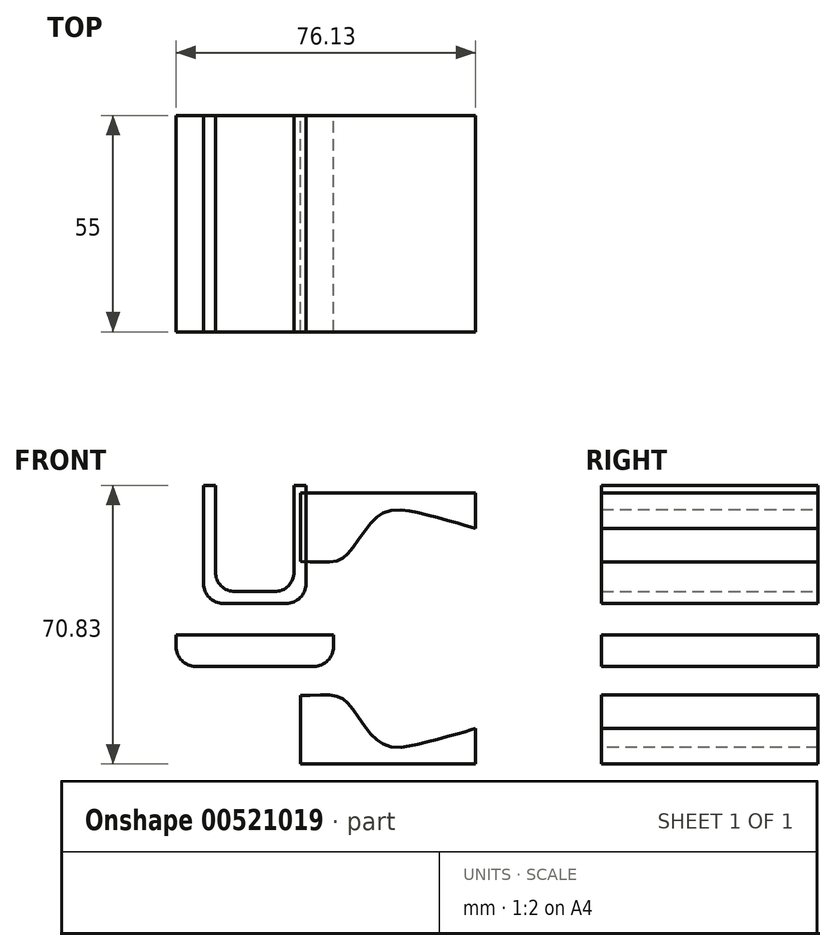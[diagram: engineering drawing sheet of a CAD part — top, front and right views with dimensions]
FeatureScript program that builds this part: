
annotation { "Feature Type Name" : "Feature", "Feature Type Description" : "" }
export const myFeature = defineFeature(function(context is Context, id is Id, definition is map)
    precondition{}
    {
        {
            var Q0;
            Q0=qCreatedBy(makeId("Front.planeOp"),FACE);
            var sketch = newSketch(context, id + "F0", { "sketchPlane" : qUnion([Q0])});
            skLineSegment(sketch, "E0.bottom", {"start": v(-10, 9.37) * mm, "end": v(10, 9.37) * mm});
            skLineSegment(sketch, "E0.top", {"start": v(-10, 6.37) * mm, "end": v(10, 6.37) * mm});
            skLineSegment(sketch, "E0.left", {"start": v(-10, 9.37) * mm, "end": v(-10, 6.37) * mm});
            skLineSegment(sketch, "E0.right", {"start": v(10, 9.37) * mm, "end": v(10, 6.37) * mm});
            skLineSegment(sketch, "E1.bottom", {"start": v(-4, 6.37) * mm, "end": v(4, 6.37) * mm});
            skLineSegment(sketch, "E1.top", {"start": v(-4, -1.63) * mm, "end": v(4, -1.63) * mm});
            skLineSegment(sketch, "E1.left", {"start": v(-4, 6.37) * mm, "end": v(-4, -1.63) * mm});
            skLineSegment(sketch, "E1.right", {"start": v(4, 6.37) * mm, "end": v(4, -1.63) * mm});
            skLineSegment(sketch, "E2.bottom", {"start": v(-20, -9.63) * mm, "end": v(20, -9.63) * mm});
            skLineSegment(sketch, "E2.top", {"start": v(-20, -1.63) * mm, "end": v(20, -1.63) * mm});
            skLineSegment(sketch, "E2.left", {"start": v(-20, -9.63) * mm, "end": v(-20, -1.63) * mm});
            skLineSegment(sketch, "E2.right", {"start": v(20, -9.63) * mm, "end": v(20, -1.63) * mm});
            skLineSegment(sketch, "E3.bottom", {"start": v(10, 6.37) * mm, "end": v(13, 6.37) * mm});
            skLineSegment(sketch, "E3.top", {"start": v(10, 36.37) * mm, "end": v(13, 36.37) * mm});
            skLineSegment(sketch, "E3.left", {"start": v(10, 6.37) * mm, "end": v(10, 36.37) * mm});
            skLineSegment(sketch, "E3.right", {"start": v(13, 6.37) * mm, "end": v(13, 36.37) * mm});
            skLineSegment(sketch, "E4.bottom", {"start": v(-10, 6.37) * mm, "end": v(-13, 6.37) * mm});
            skLineSegment(sketch, "E4.top", {"start": v(-10, 36.37) * mm, "end": v(-13, 36.37) * mm});
            skLineSegment(sketch, "E4.left", {"start": v(-10, 6.37) * mm, "end": v(-10, 36.37) * mm});
            skLineSegment(sketch, "E4.right", {"start": v(-13, 6.37) * mm, "end": v(-13, 36.37) * mm});
            skSolve(sketch);
        }
        {
            var Q0;
            Q0=makeQuery(id+"F0.imprint","IMPRINT",FACE,{"disambiguationData":[TD([[makeQuery(id+"F0.imprint","IMPRINT",EDGE,{"derivedFrom":sQuery(id+"F0.wireOp",EDGE,"E2.bottom")}),1.0]])]});
            var Q1;
            Q1=makeQuery(id+"F0.imprint","IMPRINT",FACE,{"disambiguationData":[TD([[makeQuery(id+"F0.imprint","IMPRINT",EDGE,{"derivedFrom":sQuery(id+"F0.wireOp",EDGE,"E1.bottom")}),-1.0]])]});
            var Q2;
            {var subQ2=sQuery(id+"F0.wireOp",EDGE,"E0.bottom");Q2=makeQuery(id+"F0.imprint","IMPRINT",FACE,{"disambiguationData":[TD([[makeQuery(id+"F0.imprint","IMPRINT",EDGE,{"derivedFrom":subQ2}),-1.0]])]});}
            var Q3;
            {var subQ3=sQuery(id+"F0.wireOp",EDGE,"E3.bottom");Q3=makeQuery(id+"F0.imprint","IMPRINT",FACE,{"disambiguationData":[TD([[makeQuery(id+"F0.imprint","IMPRINT",EDGE,{"derivedFrom":subQ3}),1.0]])]});}
            var Q4;
            {var subQ3=sQuery(id+"F0.wireOp",EDGE,"E4.bottom");Q4=makeQuery(id+"F0.imprint","IMPRINT",FACE,{"disambiguationData":[TD([[makeQuery(id+"F0.imprint","IMPRINT",EDGE,{"derivedFrom":subQ3}),-1.0]])]});}
            extrude(context, id + "F1", {"entities" : qUnion([Q0, Q1, Q2, Q3, Q4]), "endBound" : BoundingType.SYMMETRIC, "depth" : 55 * mm, "offsetDistance" : 25 * mm});
        }
        {
            var Q0;
            Q0=makeQuery(id+"F1.opExtrude","SWEPT_EDGE",EDGE,{"disambiguationData":[OSD([sQuery(id+"F0.wireOp",EDGE,"E0.bottom"),sQuery(id+"F0.wireOp",EDGE,"E4.left")])]});
            var Q1;
            Q1=makeQuery(id+"F1.opExtrude","SWEPT_EDGE",EDGE,{"disambiguationData":[OSD([sQuery(id+"F0.wireOp",EDGE,"E0.bottom"),sQuery(id+"F0.wireOp",EDGE,"E3.left")])]});
            var Q2;
            Q2=makeQuery(id+"F1.opExtrude","SWEPT_EDGE",EDGE,{"disambiguationData":[OSD([sQuery(id+"F0.wireOp",EDGE,"E4.bottom"),sQuery(id+"F0.wireOp",EDGE,"E4.right")])]});
            var Q3;
            Q3=makeQuery(id+"F1.opExtrude","SWEPT_EDGE",EDGE,{"disambiguationData":[OSD([sQuery(id+"F0.wireOp",EDGE,"E3.bottom"),sQuery(id+"F0.wireOp",EDGE,"E3.right")])]});
            var Q4;
            Q4=makeQuery(id+"F1.opExtrude","SWEPT_EDGE",EDGE,{"disambiguationData":[OSD([sQuery(id+"F0.wireOp",EDGE,"E2.bottom"),sQuery(id+"F0.wireOp",EDGE,"E2.left")])]});
            var Q5;
            Q5=makeQuery(id+"F1.opExtrude","SWEPT_EDGE",EDGE,{"disambiguationData":[OSD([sQuery(id+"F0.wireOp",EDGE,"E2.bottom"),sQuery(id+"F0.wireOp",EDGE,"E2.right")])]});
            fillet(context, id + "F2", {"entities" : qUnion([Q0, Q1, Q2, Q3, Q4, Q5]), "radius" : 5 * mm, "tangentPropagation" : true, "allowEdgeOverflow" : false});
        }
        {
            var Q0;
            Q0 = qSketchRegion(id + "F0", true);
            var sketch = newSketch(context, id + "F3", { "sketchPlane" : qUnion([Q0])});
            skFitSpline(sketch, "E5", {"points": [v(-30.87, 10.53) * mm, v(11.63, 14) * mm, v(24.13, 15.5) * mm, v(32.8, 25.83) * mm, v(39.46, 26.75) * mm, v(53.8, 23) * mm, v(56.13, 22) * mm, v(57.13, 0) * mm], "startDerivative": vector(208.32, 11.15) * mm, "endDerivative": vector(-6.45, -276.73) * mm});
            skLineSegment(sketch, "E6", {"start": v(-30.87, 10.53) * mm, "end": v(-30.87, 0) * mm});
            skLineSegment(sketch, "E7", {"start": v(-30.87, 0) * mm, "end": v(57.13, 0) * mm});
            skFitSpline(sketch, "E8.MirrorCS", {"points": [v(-30.87, -10.53) * mm, v(11.63, -14) * mm, v(24.13, -15.5) * mm, v(32.8, -25.83) * mm, v(39.46, -26.75) * mm, v(53.8, -23) * mm, v(56.13, -22) * mm, v(57.13, 0) * mm], "startDerivative": vector(208.32, -11.15) * mm, "endDerivative": vector(-6.45, 276.73) * mm});
            skLineSegment(sketch, "E9.MirrorCS", {"start": v(-30.87, -10.53) * mm, "end": v(-30.87, 0) * mm});
            skLineSegment(sketch, "E10", {"start": v(-41.52, 0) * mm, "end": v(90.5, 0) * mm, "construction": true});
            skPoint(sketch, "E11.end.orphan", {"position": v(-30.87, 22.53) * mm});
            skLineSegment(sketch, "E12.bottom", {"start": v(11.63, 14) * mm, "end": v(20.1, 14) * mm});
            skLineSegment(sketch, "E12.top", {"start": v(11.63, 34.46) * mm, "end": v(56.13, 34.46) * mm});
            skLineSegment(sketch, "E12.left", {"start": v(11.63, 14) * mm, "end": v(11.63, 34.46) * mm});
            skLineSegment(sketch, "E12.right", {"start": v(56.13, 22) * mm, "end": v(56.13, 34.46) * mm});
            skLineSegment(sketch, "E13.MirrorCS", {"start": v(11.63, -34.46) * mm, "end": v(56.13, -34.46) * mm});
            skLineSegment(sketch, "E14.MirrorCS", {"start": v(56.13, -22) * mm, "end": v(56.13, -34.46) * mm});
            skLineSegment(sketch, "E15.MirrorCS", {"start": v(11.63, -14) * mm, "end": v(11.63, -34.46) * mm});
            skFitSpline(sketch, "E16.0", {"points": [v(-31.03, 13.53) * mm, v(-26.74, 13.76) * mm, v(-20.46, 14.26) * mm, v(-12.55, 15.05) * mm, v(-6.9, 15.64) * mm, v(-1.58, 16.2) * mm, v(2.57, 16.57) * mm, v(5.69, 16.8) * mm, v(7.92, 16.92) * mm, v(9.7, 16.98) * mm, v(11.07, 17) * mm, v(12.41, 17) * mm, v(13.97, 16.96) * mm, v(15.67, 16.9) * mm, v(17.19, 16.85) * mm, v(18.52, 16.86) * mm, v(19.66, 16.95) * mm, v(20.62, 17.12) * mm, v(21.42, 17.38) * mm, v(22.02, 17.69) * mm, v(22.49, 18) * mm, v(22.87, 18.32) * mm, v(23.29, 18.7) * mm, v(23.86, 19.3) * mm, v(24.61, 20.17) * mm, v(25.53, 21.4) * mm, v(26.47, 22.7) * mm, v(27.42, 24.06) * mm, v(28.39, 25.4) * mm, v(29.4, 26.68) * mm, v(30.33, 27.67) * mm, v(31.17, 28.4) * mm, v(31.85, 28.88) * mm, v(32.56, 29.3) * mm, v(33.56, 29.74) * mm, v(34.87, 30.08) * mm, v(36.4, 30.18) * mm, v(37.85, 30.08) * mm, v(39.06, 29.89) * mm, v(40.05, 29.7) * mm, v(41.07, 29.48) * mm, v(42.43, 29.17) * mm, v(44.14, 28.75) * mm, v(45.9, 28.3) * mm, v(47.66, 27.83) * mm, v(49.37, 27.36) * mm, v(51, 26.91) * mm, v(52.23, 26.56) * mm, v(53.13, 26.3) * mm, v(53.75, 26.13) * mm, v(54.31, 25.97) * mm, v(54.8, 25.83) * mm, v(55.26, 25.7) * mm, v(55.7, 25.58) * mm, v(56.14, 25.43) * mm, v(56.62, 25.24) * mm, v(57.13, 24.99) * mm, v(57.67, 24.65) * mm, v(58.18, 24.22) * mm, v(58.6, 23.74) * mm, v(58.98, 23.2) * mm, v(59.38, 22.46) * mm, v(59.72, 21.5) * mm, v(59.98, 20.3) * mm, v(60.15, 18.93) * mm, v(60.3, 16.82) * mm, v(60.36, 13.45) * mm, v(60.3, 7.84) * mm, v(60.2, 2.82) * mm, v(60.13, -0.07) * mm]});
            skPoint(sketch, "E17", {"position": v(56.13, 25.43) * mm});
            skFitSpline(sketch, "E18.trimOffspring", {"points": [v(-31.03, 13.53) * mm, v(-26.74, 13.76) * mm, v(-20.46, 14.26) * mm, v(-12.55, 15.05) * mm, v(-6.9, 15.64) * mm, v(-1.58, 16.2) * mm, v(2.57, 16.57) * mm, v(5.69, 16.8) * mm, v(7.92, 16.92) * mm, v(9.7, 16.98) * mm, v(11.07, 17) * mm, v(12.41, 17) * mm, v(13.97, 16.96) * mm, v(15.67, 16.9) * mm, v(17.19, 16.85) * mm, v(18.52, 16.86) * mm, v(19.66, 16.95) * mm, v(20.62, 17.12) * mm, v(21.42, 17.38) * mm, v(22.02, 17.69) * mm, v(22.49, 18) * mm, v(22.87, 18.32) * mm, v(23.29, 18.7) * mm, v(23.86, 19.3) * mm, v(24.61, 20.17) * mm, v(25.53, 21.4) * mm, v(26.47, 22.7) * mm, v(27.42, 24.06) * mm, v(28.39, 25.4) * mm, v(29.4, 26.68) * mm, v(30.33, 27.67) * mm, v(31.17, 28.4) * mm, v(31.85, 28.88) * mm, v(32.56, 29.3) * mm, v(33.56, 29.74) * mm, v(34.87, 30.08) * mm, v(36.4, 30.18) * mm, v(37.85, 30.08) * mm, v(39.06, 29.89) * mm, v(40.05, 29.7) * mm, v(41.07, 29.48) * mm, v(42.43, 29.17) * mm, v(44.14, 28.75) * mm, v(45.9, 28.3) * mm, v(47.66, 27.83) * mm, v(49.37, 27.36) * mm, v(51, 26.91) * mm, v(52.23, 26.56) * mm, v(53.13, 26.3) * mm, v(53.75, 26.13) * mm, v(54.31, 25.97) * mm, v(54.8, 25.83) * mm, v(55.26, 25.7) * mm, v(55.7, 25.58) * mm, v(56.14, 25.43) * mm, v(56.62, 25.24) * mm, v(57.13, 24.99) * mm, v(57.67, 24.65) * mm, v(58.18, 24.22) * mm, v(58.6, 23.74) * mm, v(58.98, 23.2) * mm, v(59.38, 22.46) * mm, v(59.72, 21.5) * mm, v(59.98, 20.3) * mm, v(60.15, 18.93) * mm, v(60.3, 16.82) * mm, v(60.36, 13.45) * mm, v(60.3, 7.84) * mm, v(60.2, 2.82) * mm, v(60.13, -0.07) * mm]});
            skPoint(sketch, "E19", {"position": v(11.63, 17) * mm});
            skFitSpline(sketch, "E20.0", {"points": [v(-31.03, -13.53) * mm, v(-26.74, -13.76) * mm, v(-20.46, -14.26) * mm, v(-12.55, -15.05) * mm, v(-6.9, -15.64) * mm, v(-1.58, -16.2) * mm, v(2.57, -16.57) * mm, v(5.69, -16.8) * mm, v(7.92, -16.92) * mm, v(9.7, -16.98) * mm, v(11.07, -17) * mm, v(12.41, -17) * mm, v(13.97, -16.96) * mm, v(15.67, -16.9) * mm, v(17.19, -16.85) * mm, v(18.52, -16.86) * mm, v(19.66, -16.95) * mm, v(20.62, -17.12) * mm, v(21.42, -17.38) * mm, v(22.02, -17.69) * mm, v(22.49, -18) * mm, v(22.87, -18.32) * mm, v(23.29, -18.7) * mm, v(23.86, -19.3) * mm, v(24.61, -20.17) * mm, v(25.53, -21.4) * mm, v(26.47, -22.7) * mm, v(27.42, -24.06) * mm, v(28.39, -25.4) * mm, v(29.4, -26.68) * mm, v(30.33, -27.67) * mm, v(31.17, -28.4) * mm, v(31.85, -28.88) * mm, v(32.56, -29.3) * mm, v(33.56, -29.74) * mm, v(34.87, -30.08) * mm, v(36.4, -30.18) * mm, v(37.85, -30.08) * mm, v(39.06, -29.89) * mm, v(40.05, -29.7) * mm, v(41.07, -29.48) * mm, v(42.43, -29.17) * mm, v(44.14, -28.75) * mm, v(45.9, -28.3) * mm, v(47.66, -27.83) * mm, v(49.37, -27.36) * mm, v(51, -26.91) * mm, v(52.23, -26.56) * mm, v(53.13, -26.3) * mm, v(53.75, -26.13) * mm, v(54.31, -25.97) * mm, v(54.8, -25.83) * mm, v(55.26, -25.7) * mm, v(55.7, -25.58) * mm, v(56.14, -25.43) * mm, v(56.62, -25.24) * mm, v(57.13, -24.99) * mm, v(57.67, -24.65) * mm, v(58.18, -24.22) * mm, v(58.6, -23.74) * mm, v(58.98, -23.2) * mm, v(59.38, -22.46) * mm, v(59.72, -21.5) * mm, v(59.98, -20.3) * mm, v(60.15, -18.93) * mm, v(60.3, -16.82) * mm, v(60.36, -13.45) * mm, v(60.3, -7.84) * mm, v(60.2, -2.82) * mm, v(60.13, 0.07) * mm]});
            skPoint(sketch, "E21", {"position": v(56.13, -25.43) * mm});
            skPoint(sketch, "E22", {"position": v(11.63, -17) * mm});
            skFitSpline(sketch, "E23.trimOffspring", {"points": [v(-31.03, -13.53) * mm, v(-26.74, -13.76) * mm, v(-20.46, -14.26) * mm, v(-12.55, -15.05) * mm, v(-6.9, -15.64) * mm, v(-1.58, -16.2) * mm, v(2.57, -16.57) * mm, v(5.69, -16.8) * mm, v(7.92, -16.92) * mm, v(9.7, -16.98) * mm, v(11.07, -17) * mm, v(12.41, -17) * mm, v(13.97, -16.96) * mm, v(15.67, -16.9) * mm, v(17.19, -16.85) * mm, v(18.52, -16.86) * mm, v(19.66, -16.95) * mm, v(20.62, -17.12) * mm, v(21.42, -17.38) * mm, v(22.02, -17.69) * mm, v(22.49, -18) * mm, v(22.87, -18.32) * mm, v(23.29, -18.7) * mm, v(23.86, -19.3) * mm, v(24.61, -20.17) * mm, v(25.53, -21.4) * mm, v(26.47, -22.7) * mm, v(27.42, -24.06) * mm, v(28.39, -25.4) * mm, v(29.4, -26.68) * mm, v(30.33, -27.67) * mm, v(31.17, -28.4) * mm, v(31.85, -28.88) * mm, v(32.56, -29.3) * mm, v(33.56, -29.74) * mm, v(34.87, -30.08) * mm, v(36.4, -30.18) * mm, v(37.85, -30.08) * mm, v(39.06, -29.89) * mm, v(40.05, -29.7) * mm, v(41.07, -29.48) * mm, v(42.43, -29.17) * mm, v(44.14, -28.75) * mm, v(45.9, -28.3) * mm, v(47.66, -27.83) * mm, v(49.37, -27.36) * mm, v(51, -26.91) * mm, v(52.23, -26.56) * mm, v(53.13, -26.3) * mm, v(53.75, -26.13) * mm, v(54.31, -25.97) * mm, v(54.8, -25.83) * mm, v(55.26, -25.7) * mm, v(55.7, -25.58) * mm, v(56.14, -25.43) * mm, v(56.62, -25.24) * mm, v(57.13, -24.99) * mm, v(57.67, -24.65) * mm, v(58.18, -24.22) * mm, v(58.6, -23.74) * mm, v(58.98, -23.2) * mm, v(59.38, -22.46) * mm, v(59.72, -21.5) * mm, v(59.98, -20.3) * mm, v(60.15, -18.93) * mm, v(60.3, -16.82) * mm, v(60.36, -13.45) * mm, v(60.3, -7.84) * mm, v(60.2, -2.82) * mm, v(60.13, 0.07) * mm]});
            skSolve(sketch);
        }
        {
            var Q0;
            {var subQ0=sQuery(id+"F3.wireOp",EDGE,"E12.right");var subQ1=sQuery(id+"F3.wireOp",EDGE,"E12.top");var subQ2=makeQuery(id+"F3.imprint","INTERSECT",VERTEX,{"derivedFrom":[subQ1,subQ0]});Q0=makeQuery(id+"F3.imprint","IMPRINT",FACE,{"disambiguationData":[TD([[makeQuery(id+"F3.imprint","IMPRINT",EDGE,{"disambiguationData":[TD([[subQ2,1.0]])],"derivedFrom":subQ1}),-1.0]])]});}
            var Q1;
            {var subQ0=sQuery(id+"F3.wireOp",EDGE,"E13.MirrorCS");Q1=makeQuery(id+"F3.imprint","IMPRINT",FACE,{"disambiguationData":[TD([[makeQuery(id+"F3.imprint","IMPRINT",EDGE,{"derivedFrom":subQ0}),1.0]])]});}
            extrude(context, id + "F4", {"entities" : qUnion([Q0, Q1]), "endBound" : BoundingType.SYMMETRIC, "depth" : 55 * mm, "offsetDistance" : 25 * mm});
        }
    });
